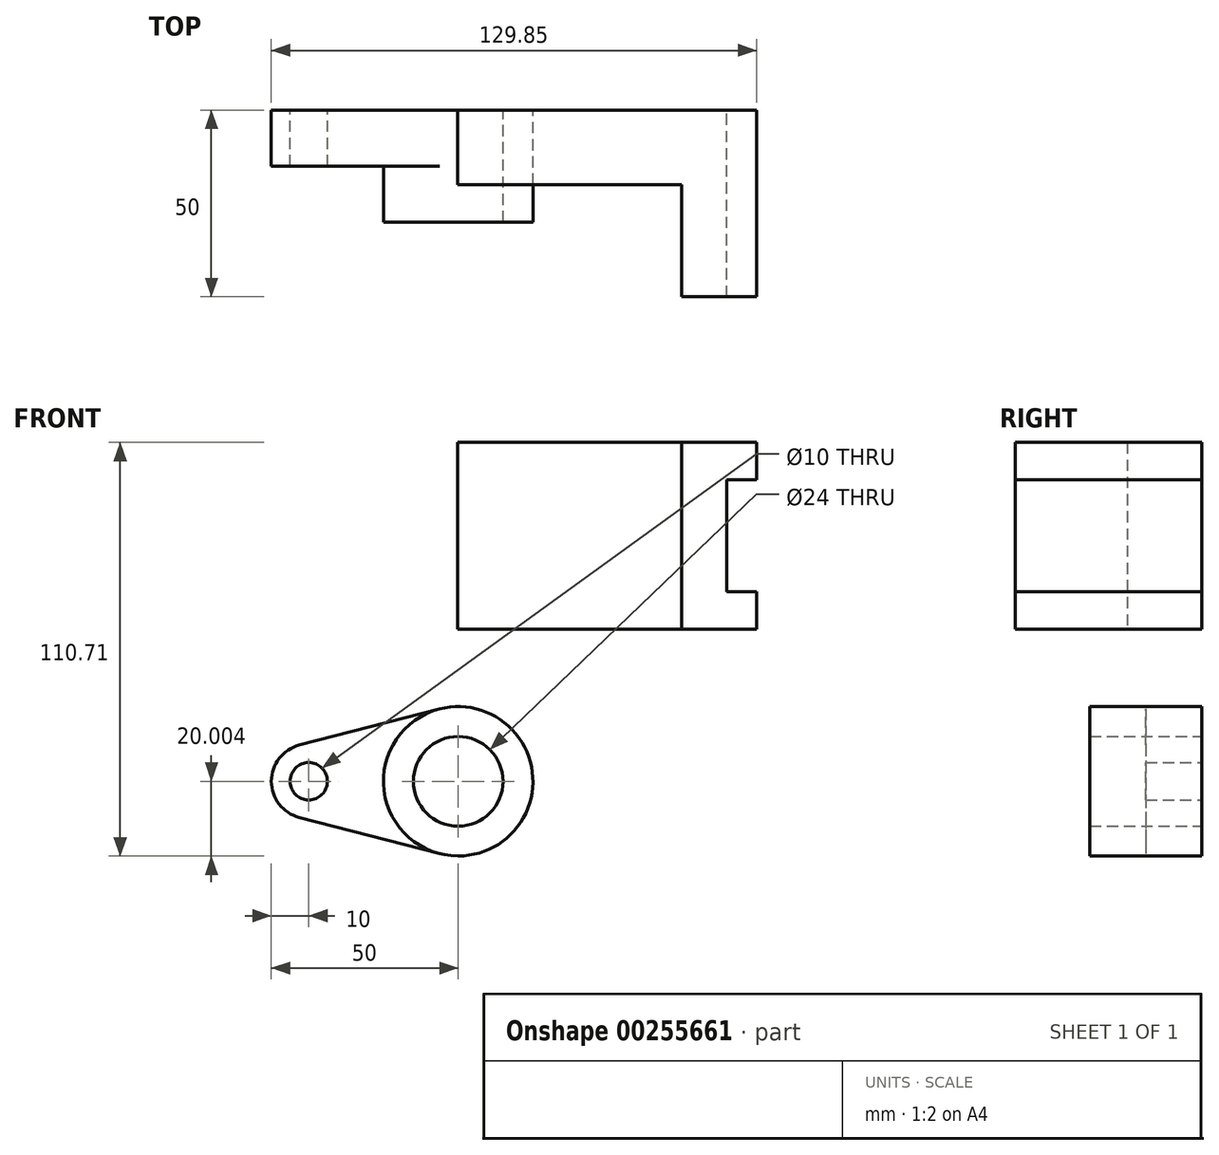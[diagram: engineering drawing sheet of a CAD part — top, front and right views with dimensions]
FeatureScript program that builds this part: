
annotation { "Feature Type Name" : "Feature", "Feature Type Description" : "" }
export const myFeature = defineFeature(function(context is Context, id is Id, definition is map)
    precondition{}
    {
        {
            var Q0;
            Q0=qCreatedBy(makeId("Front.planeOp"),FACE);
            var sketch = newSketch(context, id + "F0", { "sketchPlane" : qUnion([Q0])});
            skLineSegment(sketch, "E0.bottom", {"start": v(-0.15, 50.27) * mm, "end": v(79.85, 50.27) * mm});
            skLineSegment(sketch, "E0.top", {"start": v(-0.15, 0.27) * mm, "end": v(79.85, 0.27) * mm});
            skLineSegment(sketch, "E0.left", {"start": v(-0.15, 50.27) * mm, "end": v(-0.15, 0.27) * mm});
            skLineSegment(sketch, "E1.bottom", {"start": v(79.85, 40.27) * mm, "end": v(71.85, 40.27) * mm});
            skLineSegment(sketch, "E1.top", {"start": v(79.85, 10.27) * mm, "end": v(71.85, 10.27) * mm});
            skLineSegment(sketch, "E1.right", {"start": v(71.85, 40.27) * mm, "end": v(71.85, 10.27) * mm});
            skLineSegment(sketch, "E2", {"start": v(59.85, 50.27) * mm, "end": v(59.85, 0.27) * mm});
            skLineSegment(sketch, "E3", {"start": v(79.85, 40.27) * mm, "end": v(79.85, 50.27) * mm});
            skLineSegment(sketch, "E4", {"start": v(79.85, 0.27) * mm, "end": v(79.85, 10.27) * mm});
            skCircle(sketch, "E5", {"center": v(-40, -40.44) * mm, "radius": 5 * mm});
            skArc(sketch, "E6", {"start": v(-42.5, -30.75) * mm, "mid": v(-50, -40.44) * mm, "end": v(-42.5, -50.12) * mm});
            skCircle(sketch, "E7", {"center": v(0, -40.44) * mm, "radius": 12 * mm});
            skCircle(sketch, "E8", {"center": v(0, -40.44) * mm, "radius": 20 * mm});
            skLineSegment(sketch, "E9", {"start": v(-42.5, -30.75) * mm, "end": v(-5, -21.07) * mm});
            skLineSegment(sketch, "E10", {"start": v(-42.5, -50.12) * mm, "end": v(-5, -59.8) * mm});
            skSolve(sketch);
        }
        {
            var Q0;
            {var subQ0=sQuery(id+"F0.wireOp",EDGE,"E0.left");Q0=makeQuery(id+"F0.imprint","IMPRINT",FACE,{"disambiguationData":[TD([[makeQuery(id+"F0.imprint","IMPRINT",EDGE,{"derivedFrom":subQ0}),1.0]])]});}
            extrude(context, id + "F1", {"entities" : qUnion([Q0]), "depth" : 20 * mm});
        }
        {
            var Q0;
            Q0=makeQuery(id+"F0.imprint","IMPRINT",FACE,{"disambiguationData":[TD([[makeQuery(id+"F0.imprint","IMPRINT",EDGE,{"derivedFrom":sQuery(id+"F0.wireOp",EDGE,"E1.bottom")}),-1.0]])]});
            extrude(context, id + "F2", {"entities" : qUnion([Q0]), "operationType" : NewBodyOperationType.ADD, "depth" : 50 * mm});
        }
        {
            var Q0;
            Q0=makeQuery(id+"F0.imprint","IMPRINT",FACE,{"disambiguationData":[TD([[makeQuery(id+"F0.imprint","IMPRINT",EDGE,{"derivedFrom":sQuery(id+"F0.wireOp",EDGE,"E5")}),-1.0]])]});
            extrude(context, id + "F3", {"entities" : qUnion([Q0]), "depth" : 15 * mm});
        }
        {
            var Q0;
            Q0=makeQuery(id+"F0.imprint","IMPRINT",FACE,{"disambiguationData":[TD([[makeQuery(id+"F0.imprint","IMPRINT",EDGE,{"derivedFrom":sQuery(id+"F0.wireOp",EDGE,"E7")}),-1.0]])]});
            extrude(context, id + "F4", {"entities" : qUnion([Q0]), "operationType" : NewBodyOperationType.ADD, "depth" : 30 * mm});
        }
    });
